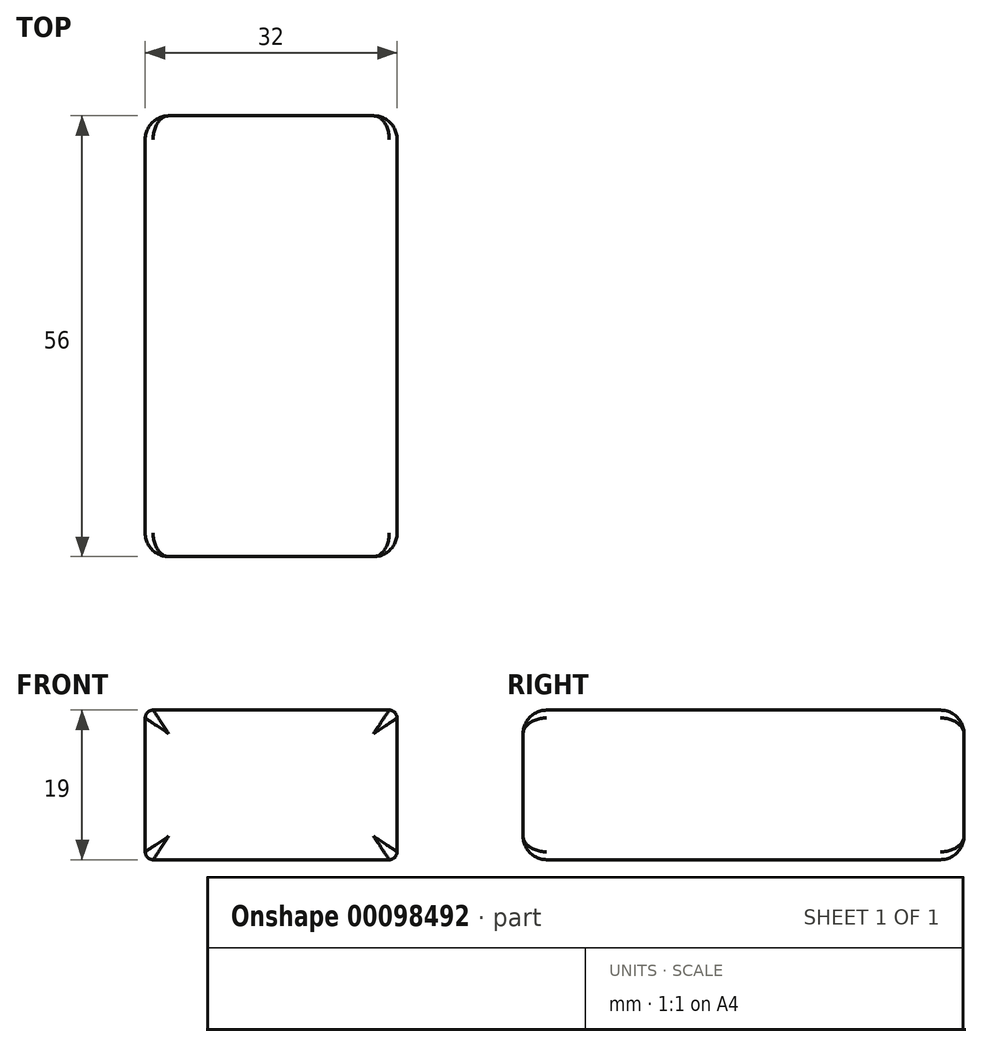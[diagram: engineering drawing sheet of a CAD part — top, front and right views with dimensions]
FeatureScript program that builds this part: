
annotation { "Feature Type Name" : "Feature", "Feature Type Description" : "" }
export const myFeature = defineFeature(function(context is Context, id is Id, definition is map)
    precondition{}
    {
        {
            var Q0;
            Q0=qCreatedBy(makeId("Top.planeOp"),FACE);
            var sketch = newSketch(context, id + "F0", { "sketchPlane" : qUnion([Q0])});
            skLineSegment(sketch, "E0.bottom", {"start": v(16, -28) * mm, "end": v(-16, -28) * mm});
            skLineSegment(sketch, "E0.top", {"start": v(16, 28) * mm, "end": v(-16, 28) * mm});
            skLineSegment(sketch, "E0.left", {"start": v(16, -28) * mm, "end": v(16, 28) * mm});
            skLineSegment(sketch, "E0.right", {"start": v(-16, -28) * mm, "end": v(-16, 28) * mm});
            skPoint(sketch, "E0.middle", {"position": v(0, 0) * mm});
            skSolve(sketch);
        }
        {
            var Q0;
            Q0=qSketchRegion(id+"F0",true);
            extrude(context, id + "F1", {"entities" : qUnion([Q0]), "depth" : 19 * mm});
        }
        {
            var Q0;
            Q0=makeQuery(id+"F1.opExtrude","CAP_EDGE",EDGE,{"disambiguationData":[OSD([sQuery(id+"F0.wireOp",EDGE,"E0.left")])],"isStart":false});
            var Q1;
            Q1=makeQuery(id+"F1.opExtrude","CAP_EDGE",EDGE,{"disambiguationData":[OSD([sQuery(id+"F0.wireOp",EDGE,"E0.left")])],"isStart":true});
            var Q2;
            Q2=makeQuery(id+"F1.opExtrude","CAP_EDGE",EDGE,{"disambiguationData":[OSD([sQuery(id+"F0.wireOp",EDGE,"E0.right")])],"isStart":false});
            var Q3;
            Q3=makeQuery(id+"F1.opExtrude","CAP_EDGE",EDGE,{"disambiguationData":[OSD([sQuery(id+"F0.wireOp",EDGE,"E0.right")])],"isStart":true});
            fillet(context, id + "F2", {"entities" : qUnion([Q0, Q1, Q2, Q3]), "radius" : 1 * mm, "tangentPropagation" : true, "allowEdgeOverflow" : false});
        }
        {
            var Q0;
            Q0=makeQuery(id+"F1.opExtrude","CAP_EDGE",EDGE,{"disambiguationData":[OSD([sQuery(id+"F0.wireOp",EDGE,"E0.top")])],"isStart":true});
            var Q1;
            Q1=makeQuery(id+"F1.opExtrude","CAP_EDGE",EDGE,{"disambiguationData":[OSD([sQuery(id+"F0.wireOp",EDGE,"E0.bottom")])],"isStart":true});
            fillet(context, id + "F3", {"entities" : qUnion([Q0, Q1]), "radius" : 3 * mm, "tangentPropagation" : true, "allowEdgeOverflow" : false});
        }
    });
